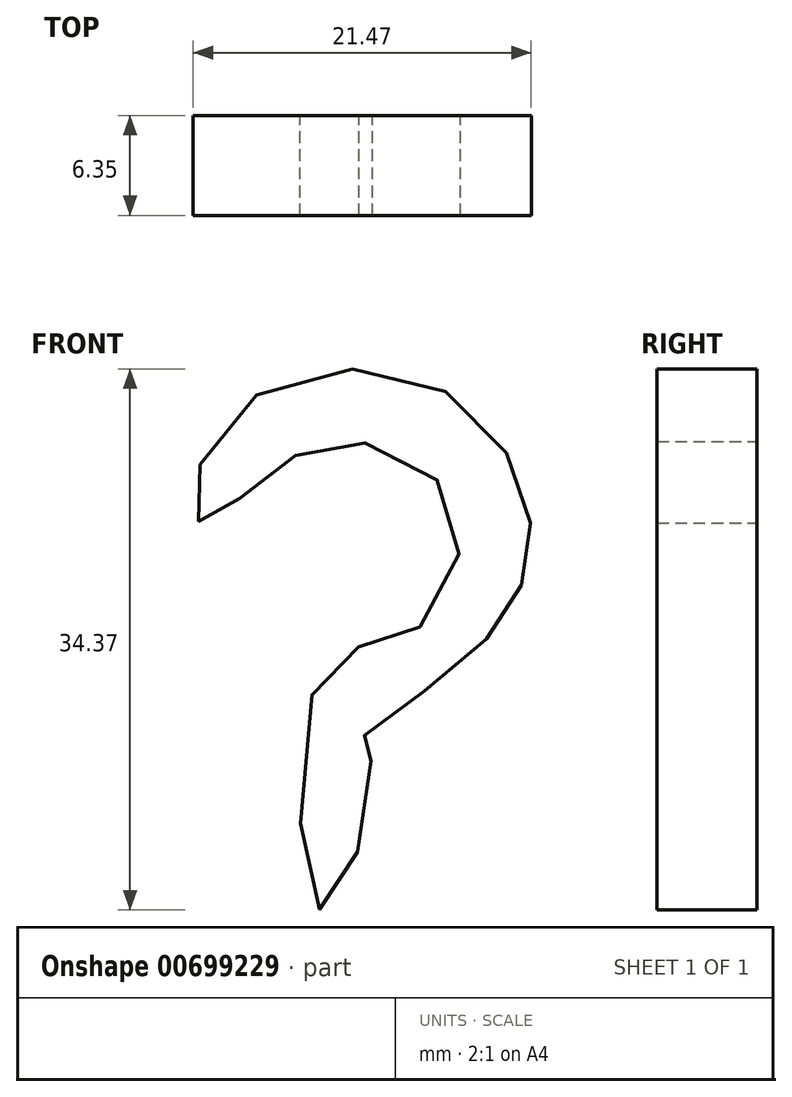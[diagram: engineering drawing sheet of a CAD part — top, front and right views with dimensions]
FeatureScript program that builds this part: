
annotation { "Feature Type Name" : "Feature", "Feature Type Description" : "" }
export const myFeature = defineFeature(function(context is Context, id is Id, definition is map)
    precondition{}
    {
        {
            var Q0;
            Q0=qCreatedBy(makeId("Front.planeOp"),FACE);
            var sketch = newSketch(context, id + "F0", { "sketchPlane" : qUnion([Q0])});
            skFitSpline(sketch, "E0", {"points": [v(11.03, 55.87) * mm, v(14.16, 57.82) * mm, v(20.43, 60.96) * mm, v(27.48, 56.26) * mm, v(23.96, 48.42) * mm, v(18.87, 46.46) * mm, v(18.87, 31.19) * mm, v(22, 40.59) * mm, v(21.22, 41.76) * mm, v(26.7, 46.07) * mm, v(31.4, 51.56) * mm, v(31.8, 57.43) * mm, v(25.13, 64.87) * mm, v(12.6, 62.13) * mm, v(11.03, 55.87) * mm]});
            skSolve(sketch);
        }
        {
            var Q0;
            Q0=makeQuery(id+"F0.imprint","IMPRINT",FACE,{"disambiguationData":[TD([[makeQuery(id+"F0.imprint","IMPRINT",EDGE,{"derivedFrom":sQuery(id+"F0.wireOp",EDGE,"E0")}),1.0]])]});
            extrude(context, id + "F1", {"entities" : qUnion([Q0]), "depth" : 6.35 * mm, "offsetDistance" : 25.4 * mm});
        }
    });
